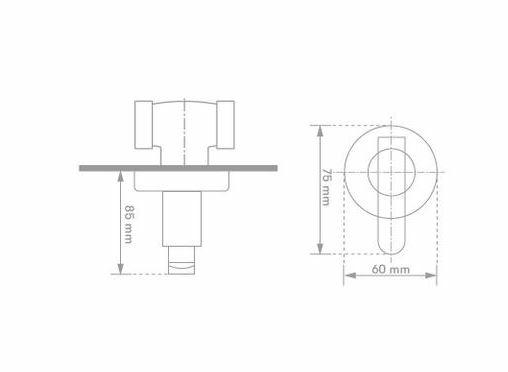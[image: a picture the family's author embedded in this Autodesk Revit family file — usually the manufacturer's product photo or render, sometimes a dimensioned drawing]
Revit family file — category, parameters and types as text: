
# Revit family: 01-1635-11 MEZCLADOR DUCHA 8” SIN SALIDA TINA HELIX CRUZ
name_source: partatom
category: Plumbing Fixtures
revit_build: Autodesk Revit 2018 (Build: 20170223_1515(x64)
units: mm (PartAtom-declared; Revit-internal decimal feet)

## family parameters
Cut with Voids When Loaded = No
Host = Face
OmniClass Number = 23.31.11.00
Part Type = Normal
Room Calculation Point = No
Round Connector Dimension = Use Diameter
Shared = No

## types (1)
- 01-1635-11
    Alto Manija = 85 mm  [stored 0.278871 ft]
    Ancho manija = 66 mm  [stored 0.216535 ft]
    CW Connection = Yes
    Default Elevation = 0 mm  [stored 0 ft]
    Description = Mezclador ducha
    Distancia entre griferias = 203 mm
    Escudo = 60 mm  [stored 0.19685 ft]
    HW Connection = Yes
    Link Ficha Tecnica = https://infotecnica.gricol.com
    Manufacturer = Gricol
    Model = 01-1635-11
    Plastico ABS Cromado = Plastico - ABS Cromado
    Product Name = MEZCLADOR DUCHA 8 SST HELIX PALA
    Type Image = <None>
    URL = https://www.gricol.com
    Vent Connection = No
    Waste Connection = No

note: [stored X ft] marks values corroborated as IEEE doubles in the binary element streams (Revit-internal decimal feet)

## geometry (parser evidence)
native form markers: Blend x2, Sweep x24
no freeform markers — native parametric forms only
